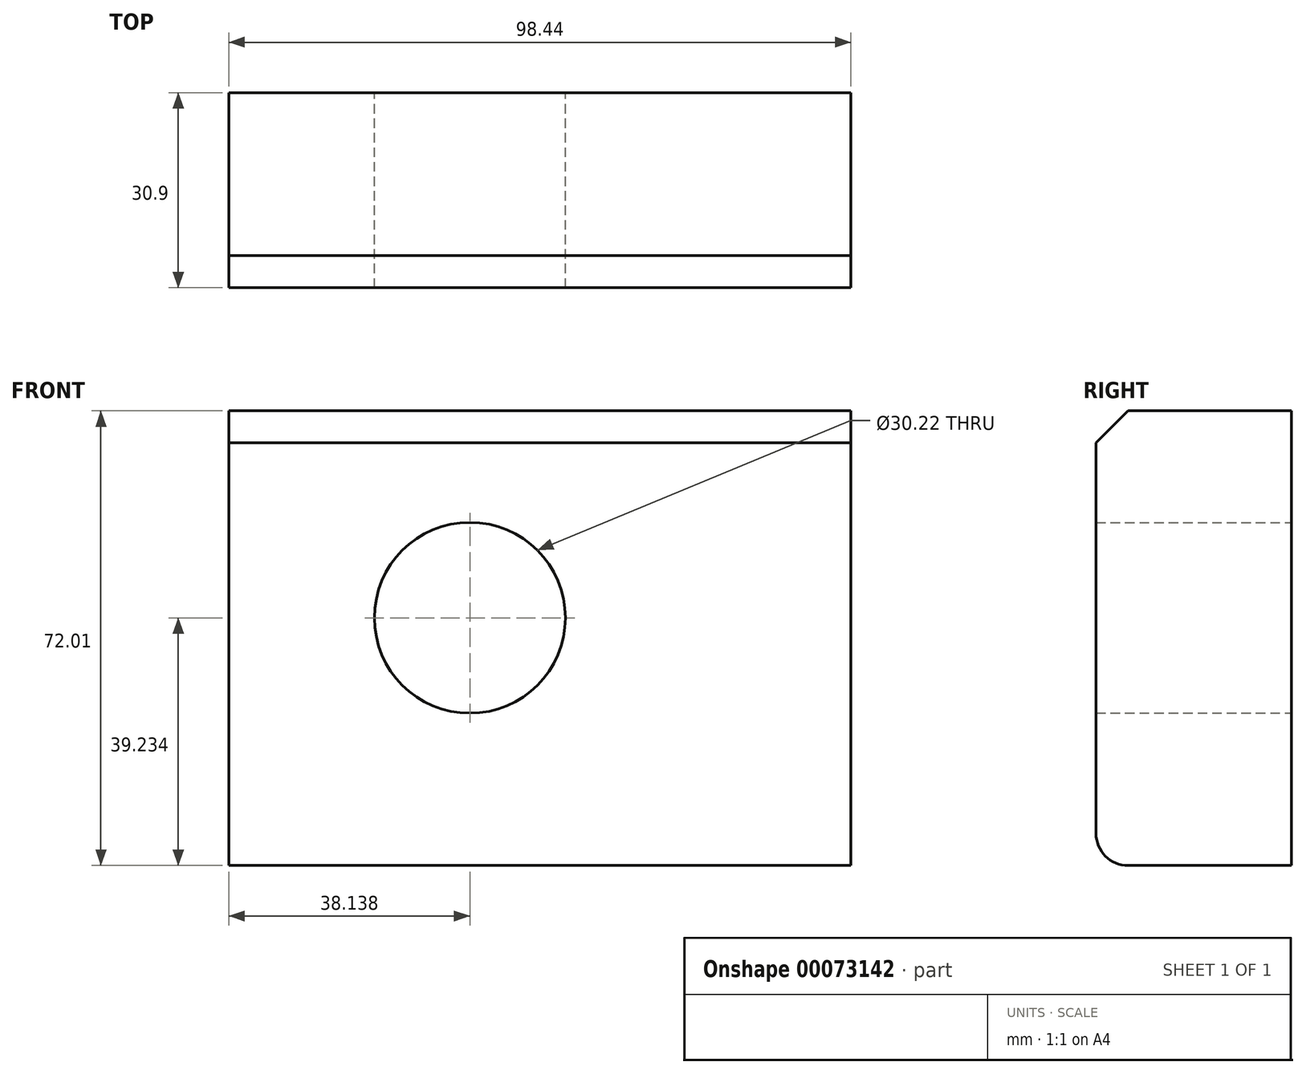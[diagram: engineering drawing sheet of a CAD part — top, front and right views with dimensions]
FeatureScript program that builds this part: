
annotation { "Feature Type Name" : "Feature", "Feature Type Description" : "" }
export const myFeature = defineFeature(function(context is Context, id is Id, definition is map)
    precondition{}
    {
        {
            var Q0;
            Q0=qCreatedBy(makeId("Front.planeOp"),FACE);
            var sketch = newSketch(context, id + "F0", { "sketchPlane" : qUnion([Q0])});
            skLineSegment(sketch, "E0.bottom", {"start": v(-65.58, 42.2) * mm, "end": v(32.86, 42.2) * mm});
            skLineSegment(sketch, "E0.top", {"start": v(-65.58, -29.82) * mm, "end": v(32.86, -29.82) * mm});
            skLineSegment(sketch, "E0.left", {"start": v(-65.58, 42.2) * mm, "end": v(-65.58, -29.82) * mm});
            skLineSegment(sketch, "E0.right", {"start": v(32.86, 42.2) * mm, "end": v(32.86, -29.82) * mm});
            skCircle(sketch, "E1", {"center": v(-27.44, 9.41) * mm, "radius": 15.1 * mm});
            skSolve(sketch);
        }
        {
            var Q0;
            Q0 = qSketchRegion(id + "F0", true);
            var Q1;
            Q1=sQuery(id+"F0.wireOp",EDGE,"E0.top");
            extrude(context, id + "F1", {"entities" : qUnion([Q0]), "surfaceEntities" : qUnion([Q1]), "depth" : 30.9 * mm});
        }
        {
            var Q0;
            Q0=makeQuery(id+"F1.opExtrude","CAP_EDGE",EDGE,{"disambiguationData":[OSD([sQuery(id+"F0.wireOp",EDGE,"E0.top")])],"isStart":false});
            fillet(context, id + "F2", {"entities" : qUnion([Q0]), "radius" : 5.08 * mm, "tangentPropagation" : true, "allowEdgeOverflow" : false});
        }
        {
            var Q0;
            Q0=makeQuery(id+"F1.opExtrude","CAP_EDGE",EDGE,{"disambiguationData":[OSD([sQuery(id+"F0.wireOp",EDGE,"E0.bottom")])],"isStart":false});
            chamfer(context, id + "F3", {"entities" : qUnion([Q0]), "width" : 5.08 * mm, "tangentPropagation" : true});
        }
    });
